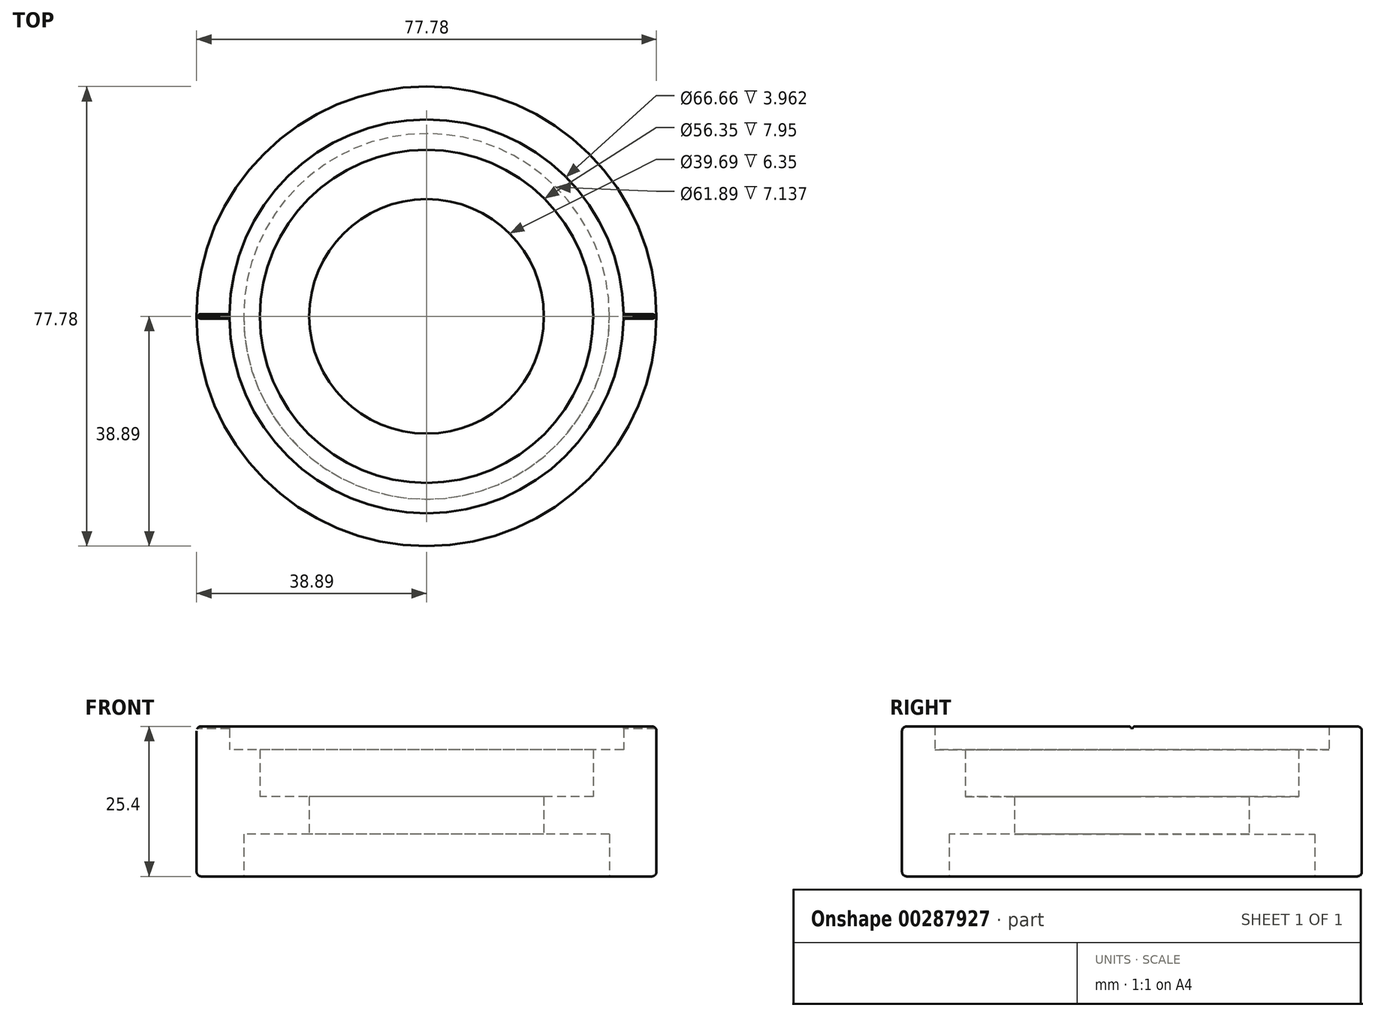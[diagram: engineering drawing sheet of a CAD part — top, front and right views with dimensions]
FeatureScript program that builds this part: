
annotation { "Feature Type Name" : "Feature", "Feature Type Description" : "" }
export const myFeature = defineFeature(function(context is Context, id is Id, definition is map)
    precondition{}
    {
        {
            var Q0;
            Q0=qCreatedBy(makeId("Top.planeOp"),FACE);
            var sketch = newSketch(context, id + "F0", { "sketchPlane" : qUnion([Q0])});
            skCircle(sketch, "E0", {"center": v(0, 0) * mm, "radius": 38.9 * mm});
            skCircle(sketch, "E1", {"center": v(0, 0) * mm, "radius": 33.33 * mm});
            skCircle(sketch, "E2", {"center": v(0, 0) * mm, "radius": 28.17 * mm});
            skCircle(sketch, "E3", {"center": v(0, 0) * mm, "radius": 19.84 * mm});
            skSolve(sketch);
        }
        {
            var Q0;
            Q0=makeQuery(id+"F0.imprint","IMPRINT",FACE,{"disambiguationData":[TD([[makeQuery(id+"F0.imprint","IMPRINT",EDGE,{"derivedFrom":sQuery(id+"F0.wireOp",EDGE,"E0")}),1.0]])]});
            extrude(context, id + "F1", {"entities" : qUnion([Q0]), "depth" : 25.4 * mm, "offsetDistance" : 25.4 * mm});
        }
        {
            var Q0;
            Q0=makeQuery(id+"F0.imprint","IMPRINT",FACE,{"disambiguationData":[TD([[makeQuery(id+"F0.imprint","IMPRINT",EDGE,{"derivedFrom":sQuery(id+"F0.wireOp",EDGE,"E1")}),1.0]])]});
            var Q1;
            Q1=makeQuery(id+"F1.opExtrude","CAP_FACE",FACE,{"disambiguationData":[OSD([sQuery(id+"F0.wireOp",EDGE,"E0"),sQuery(id+"F0.wireOp",EDGE,"E1")])],"isStart":false});
            extrude(context, id + "F2", {"entities" : qUnion([Q0]), "operationType" : NewBodyOperationType.ADD, "endBound" : BoundingType.UP_TO_SURFACE, "depth" : 25.4 * mm, "endBoundEntityFace" : qUnion([Q1]), "hasOffset" : true, "offsetDistance" : 3.96 * mm});
        }
        {
            var Q0;
            Q0=makeQuery(id+"F0.imprint","IMPRINT",FACE,{"disambiguationData":[TD([[makeQuery(id+"F0.imprint","IMPRINT",EDGE,{"derivedFrom":sQuery(id+"F0.wireOp",EDGE,"E2")}),1.0]])]});
            var Q1;
            Q1=makeQuery(id+"F1.opExtrude","CAP_FACE",FACE,{"disambiguationData":[OSD([sQuery(id+"F0.wireOp",EDGE,"E0"),sQuery(id+"F0.wireOp",EDGE,"E1")])],"isStart":false});
            extrude(context, id + "F3", {"entities" : qUnion([Q0]), "operationType" : NewBodyOperationType.ADD, "endBound" : BoundingType.UP_TO_SURFACE, "depth" : 25.4 * mm, "endBoundEntityFace" : qUnion([Q1]), "hasOffset" : true, "offsetDistance" : 11.9 * mm});
        }
        {
            var Q0;
            {var subQ0=sQuery(id+"F0.wireOp",EDGE,"E2");var subQ1=sQuery(id+"F0.wireOp",EDGE,"E1");Q0=makeQuery(id+"F3.boolean.opBoolean","MERGE",FACE,{"derivedFrom":[makeQuery(id+"F2.boolean.opBoolean","MERGE",FACE,{"derivedFrom":[makeQuery(id+"F1.opExtrude","CAP_FACE",FACE,{"disambiguationData":[OSD([sQuery(id+"F0.wireOp",EDGE,"E0"),subQ1])],"isStart":true}),makeQuery(id+"F2.opExtrude","CAP_FACE",FACE,{"disambiguationData":[OSD([subQ1,subQ0])],"isStart":true})]}),makeQuery(id+"F3.opExtrude","CAP_FACE",FACE,{"disambiguationData":[OSD([subQ0,sQuery(id+"F0.wireOp",EDGE,"E3")])],"isStart":true})]});}
            var sketch = newSketch(context, id + "F4", { "sketchPlane" : qUnion([Q0])});
            skCircle(sketch, "E4", {"center": v(0, 0) * mm, "radius": 30.94 * mm});
            skSolve(sketch);
        }
        {
            var Q0;
            Q0=makeQuery(id+"F4.imprint","IMPRINT",FACE,{"disambiguationData":[TD([[makeQuery(id+"F4.imprint","IMPRINT",EDGE,{"derivedFrom":sQuery(id+"F4.wireOp",EDGE,"E4")}),1.0]])]});
            var Q1;
            Q1=makeQuery(id+"F1.opExtrude","CAP_FACE",FACE,{"disambiguationData":[OSD([sQuery(id+"F0.wireOp",EDGE,"E0"),sQuery(id+"F0.wireOp",EDGE,"E1")])],"isStart":false});
            extrude(context, id + "F5", {"entities" : qUnion([Q0]), "operationType" : NewBodyOperationType.REMOVE, "endBound" : BoundingType.UP_TO_SURFACE, "oppositeDirection" : true, "depth" : 25.4 * mm, "endBoundEntityFace" : qUnion([Q1]), "hasOffset" : true, "offsetDistance" : 18.26 * mm});
        }
        {
            var Q0;
            Q0=makeQuery(id+"F1.opExtrude","CAP_EDGE",EDGE,{"disambiguationData":[OSD([sQuery(id+"F0.wireOp",EDGE,"E0")])],"isStart":false});
            var Q1;
            Q1=makeQuery(id+"F1.opExtrude","CAP_EDGE",EDGE,{"disambiguationData":[OSD([sQuery(id+"F0.wireOp",EDGE,"E0")])],"isStart":true});
            fillet(context, id + "F6", {"entities" : qUnion([Q0, Q1]), "radius" : 0.79 * mm, "tangentPropagation" : true, "allowEdgeOverflow" : false});
        }
        {
            var Q0;
            Q0=qCreatedBy(makeId("Right.planeOp"),FACE);
            cPlane(context, id + "F7", {"entities" : qUnion([Q0]), "cplaneType" : CPlaneType.OFFSET, "offset" : 38.9 * mm, "oppositeDirection" : true, "width" : 152.4 * mm, "height" : 152.4 * mm});
        }
        {
            var Q0;
            Q0=qCreatedBy(id+"F7.planeOp",FACE);
            var sketch = newSketch(context, id + "F8", { "sketchPlane" : qUnion([Q0])});
            skLineSegment(sketch, "E5", {"start": v(0.4, 25.4) * mm, "end": v(0, 25) * mm});
            skLineSegment(sketch, "E6", {"start": v(0, 25) * mm, "end": v(-0.4, 25.4) * mm});
            skLineSegment(sketch, "E7", {"start": v(0.4, 25.4) * mm, "end": v(-0.4, 25.4) * mm});
            skSolve(sketch);
        }
        {
            var Q0;
            Q0=makeQuery(id+"F8.imprint","IMPRINT",FACE,{"disambiguationData":[TD([[makeQuery(id+"F8.imprint","IMPRINT",EDGE,{"derivedFrom":sQuery(id+"F8.wireOp",EDGE,"E5")}),-1.0]])]});
            extrude(context, id + "F9", {"entities" : qUnion([Q0]), "operationType" : NewBodyOperationType.REMOVE, "depth" : 127 * mm, "offsetDistance" : 25.4 * mm});
        }
    });
